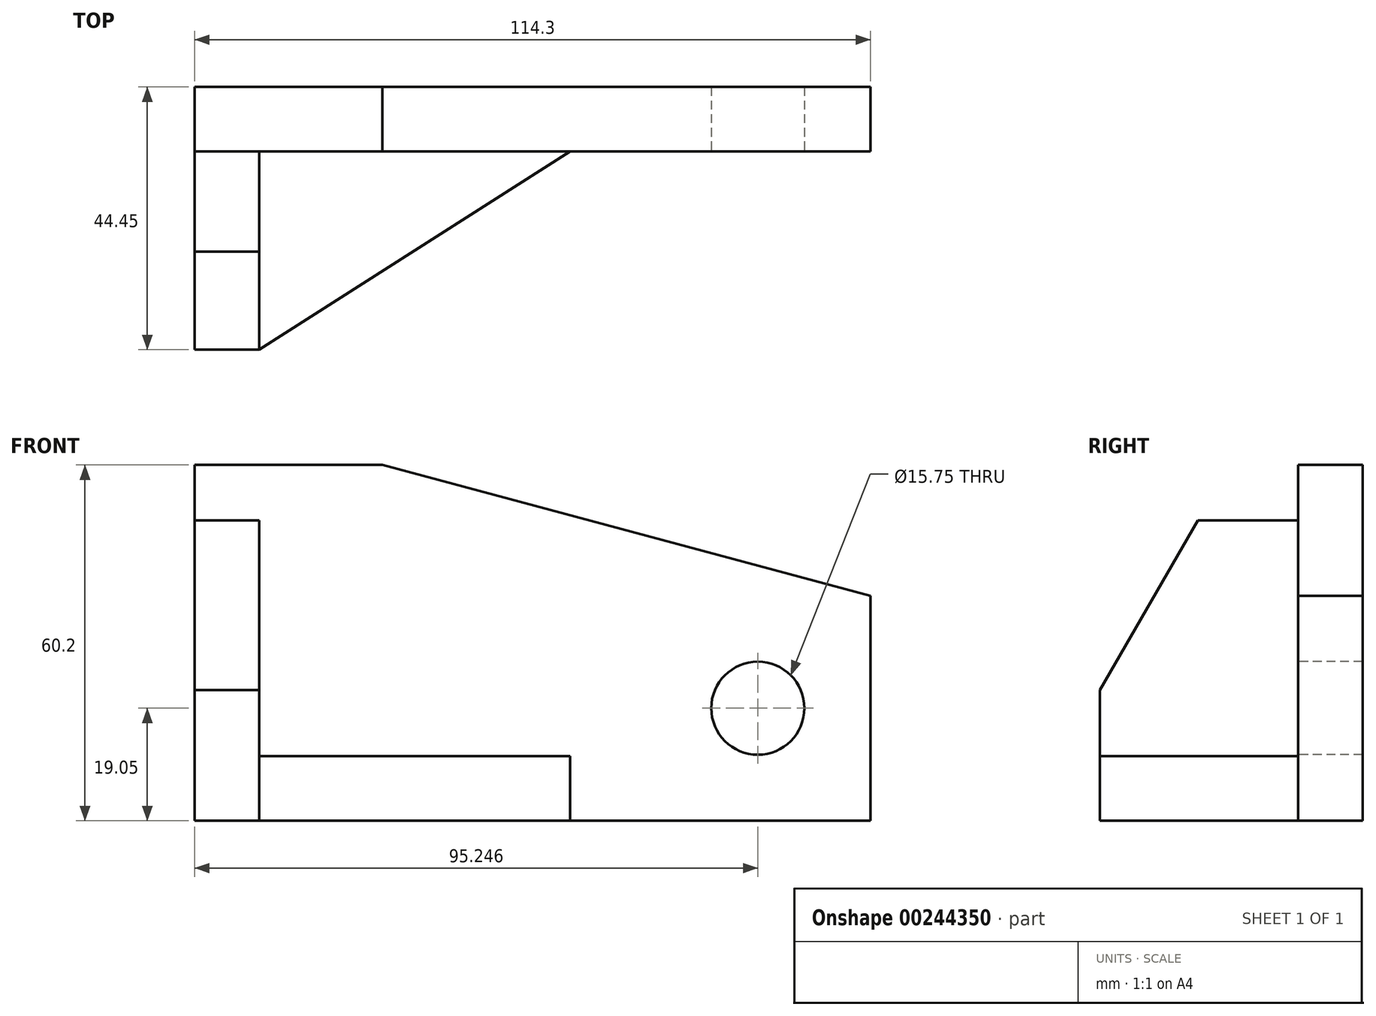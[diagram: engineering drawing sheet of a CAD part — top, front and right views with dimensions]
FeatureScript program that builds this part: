
annotation { "Feature Type Name" : "Feature", "Feature Type Description" : "" }
export const myFeature = defineFeature(function(context is Context, id is Id, definition is map)
    precondition{}
    {
        {
            var Q0;
            Q0=qCreatedBy(makeId("Top.planeOp"),FACE);
            var sketch = newSketch(context, id + "F0", { "sketchPlane" : qUnion([Q0])});
            skLineSegment(sketch, "E0", {"start": v(-64.95, 55.03) * mm, "end": v(49.35, 55.03) * mm});
            skLineSegment(sketch, "E1", {"start": v(49.35, 55.03) * mm, "end": v(49.35, 44.1) * mm});
            skLineSegment(sketch, "E2", {"start": v(49.35, 44.1) * mm, "end": v(-64.95, 44.1) * mm});
            skLineSegment(sketch, "E3", {"start": v(-64.95, 44.1) * mm, "end": v(-64.95, 55.03) * mm});
            skLineSegment(sketch, "E4", {"start": v(-64.95, 44.1) * mm, "end": v(-64.95, 10.58) * mm});
            skLineSegment(sketch, "E5", {"start": v(-64.95, 10.58) * mm, "end": v(-54.03, 10.58) * mm});
            skLineSegment(sketch, "E6", {"start": v(-54.03, 10.58) * mm, "end": v(-54.03, 44.1) * mm});
            skLineSegment(sketch, "E7", {"start": v(-54.03, 10.58) * mm, "end": v(-1.45, 44.1) * mm});
            skLineSegment(sketch, "E8", {"start": v(-54.03, 44.1) * mm, "end": v(-1.45, 44.1) * mm});
            skLineSegment(sketch, "E9", {"start": v(-64.95, 44.1) * mm, "end": v(-54.03, 44.1) * mm});
            skSolve(sketch);
        }
        {
            var Q0;
            Q0=makeQuery(id+"F0.imprint","IMPRINT",FACE,{"disambiguationData":[TD([[makeQuery(id+"F0.imprint","IMPRINT",EDGE,{"derivedFrom":sQuery(id+"F0.wireOp",EDGE,"E6")}),-1.0]])]});
            var Q1;
            Q1=makeQuery(id+"F0.imprint","IMPRINT",FACE,{"disambiguationData":[TD([[makeQuery(id+"F0.imprint","IMPRINT",EDGE,{"derivedFrom":sQuery(id+"F0.wireOp",EDGE,"E4")}),1.0]])]});
            extrude(context, id + "F1", {"entities" : qUnion([Q0, Q1]), "depth" : 10.92 * mm});
        }
        {
            var Q0;
            Q0=makeQuery(id+"F0.imprint","IMPRINT",FACE,{"disambiguationData":[TD([[makeQuery(id+"F0.imprint","IMPRINT",EDGE,{"derivedFrom":sQuery(id+"F0.wireOp",EDGE,"E0")}),-1.0]])]});
            extrude(context, id + "F2", {"entities" : qUnion([Q0]), "operationType" : NewBodyOperationType.ADD, "depth" : 60.2 * mm});
        }
        {
            var Q0;
            Q0=makeQuery(id+"F0.imprint","IMPRINT",FACE,{"disambiguationData":[TD([[makeQuery(id+"F0.imprint","IMPRINT",EDGE,{"derivedFrom":sQuery(id+"F0.wireOp",EDGE,"E4")}),1.0]])]});
            extrude(context, id + "F3", {"entities" : qUnion([Q0]), "operationType" : NewBodyOperationType.ADD, "depth" : 50.8 * mm});
        }
        {
            var Q0;
            Q0=makeQuery(id+"F2.opExtrude","SWEPT_FACE",FACE,{"disambiguationData":[OSD([sQuery(id+"F0.wireOp",EDGE,"E2"),sQuery(id+"F0.wireOp",EDGE,"E8"),sQuery(id+"F0.wireOp",EDGE,"E9")])]});
            var sketch = newSketch(context, id + "F4", { "sketchPlane" : qUnion([Q0])});
            skLineSegment(sketch, "E10", {"start": v(-64.95, 60.2) * mm, "end": v(-33.2, 60.2) * mm});
            skLineSegment(sketch, "E11", {"start": v(-33.2, 60.2) * mm, "end": v(49.35, 38.08) * mm});
            skLineSegment(sketch, "E12", {"start": v(-33.2, 60.2) * mm, "end": v(49.35, 60.2) * mm});
            skLineSegment(sketch, "E13", {"start": v(49.35, 60.2) * mm, "end": v(49.35, 38.08) * mm});
            skSolve(sketch);
        }
        {
            var Q0;
            Q0=makeQuery(id+"F4.imprint","IMPRINT",FACE,{"disambiguationData":[TD([[makeQuery(id+"F4.imprint","IMPRINT",EDGE,{"derivedFrom":sQuery(id+"F4.wireOp",EDGE,"E11")}),1.0]])]});
            extrude(context, id + "F5", {"entities" : qUnion([Q0]), "operationType" : NewBodyOperationType.REMOVE, "endBound" : BoundingType.THROUGH_ALL, "oppositeDirection" : true, "depth" : 25.4 * mm});
        }
        {
            var Q0;
            {var subQ0=sQuery(id+"F0.wireOp",EDGE,"E4");Q0=makeQuery(id+"F3.boolean.opBoolean","MERGE",FACE,{"derivedFrom":[makeQuery(id+"F2.boolean.opBoolean","MERGE",FACE,{"derivedFrom":[makeQuery(id+"F1.opExtrude","SWEPT_FACE",FACE,{"disambiguationData":[OSD([subQ0])]}),makeQuery(id+"F2.opExtrude","SWEPT_FACE",FACE,{"disambiguationData":[OSD([sQuery(id+"F0.wireOp",EDGE,"E3")])]})]}),makeQuery(id+"F3.opExtrude","SWEPT_FACE",FACE,{"disambiguationData":[OSD([subQ0])]})]});}
            var sketch = newSketch(context, id + "F6", { "sketchPlane" : qUnion([Q0])});
            skLineSegment(sketch, "E14", {"start": v(-10.58, 0) * mm, "end": v(-10.58, 22.1) * mm});
            skLineSegment(sketch, "E15", {"start": v(-10.58, 22.1) * mm, "end": v(-10.58, 50.8) * mm});
            skLineSegment(sketch, "E16", {"start": v(-10.58, 22.1) * mm, "end": v(-27.15, 50.8) * mm});
            skLineSegment(sketch, "E17", {"start": v(-27.15, 50.8) * mm, "end": v(-10.58, 50.8) * mm});
            skSolve(sketch);
        }
        {
            var Q0;
            Q0=makeQuery(id+"F6.imprint","IMPRINT",FACE,{"disambiguationData":[TD([[makeQuery(id+"F6.imprint","IMPRINT",EDGE,{"derivedFrom":sQuery(id+"F6.wireOp",EDGE,"E16")}),-1.0]])]});
            extrude(context, id + "F7", {"entities" : qUnion([Q0]), "operationType" : NewBodyOperationType.REMOVE, "endBound" : BoundingType.THROUGH_ALL, "oppositeDirection" : true, "depth" : 25.4 * mm});
        }
        {
            var Q0;
            Q0=makeQuery(id+"F2.opExtrude","SWEPT_FACE",FACE,{"disambiguationData":[OSD([sQuery(id+"F0.wireOp",EDGE,"E2"),sQuery(id+"F0.wireOp",EDGE,"E8"),sQuery(id+"F0.wireOp",EDGE,"E9")])]});
            var sketch = newSketch(context, id + "F8", { "sketchPlane" : qUnion([Q0])});
            skCircle(sketch, "E18", {"center": v(30.3, 19.05) * mm, "radius": 7.87 * mm});
            skSolve(sketch);
        }
        {
            var Q0;
            Q0=makeQuery(id+"F8.imprint","IMPRINT",FACE,{"disambiguationData":[TD([[makeQuery(id+"F8.imprint","IMPRINT",EDGE,{"derivedFrom":sQuery(id+"F8.wireOp",EDGE,"E18")}),1.0]])]});
            extrude(context, id + "F9", {"entities" : qUnion([Q0]), "operationType" : NewBodyOperationType.REMOVE, "endBound" : BoundingType.THROUGH_ALL, "oppositeDirection" : true, "depth" : 25.4 * mm});
        }
    });
